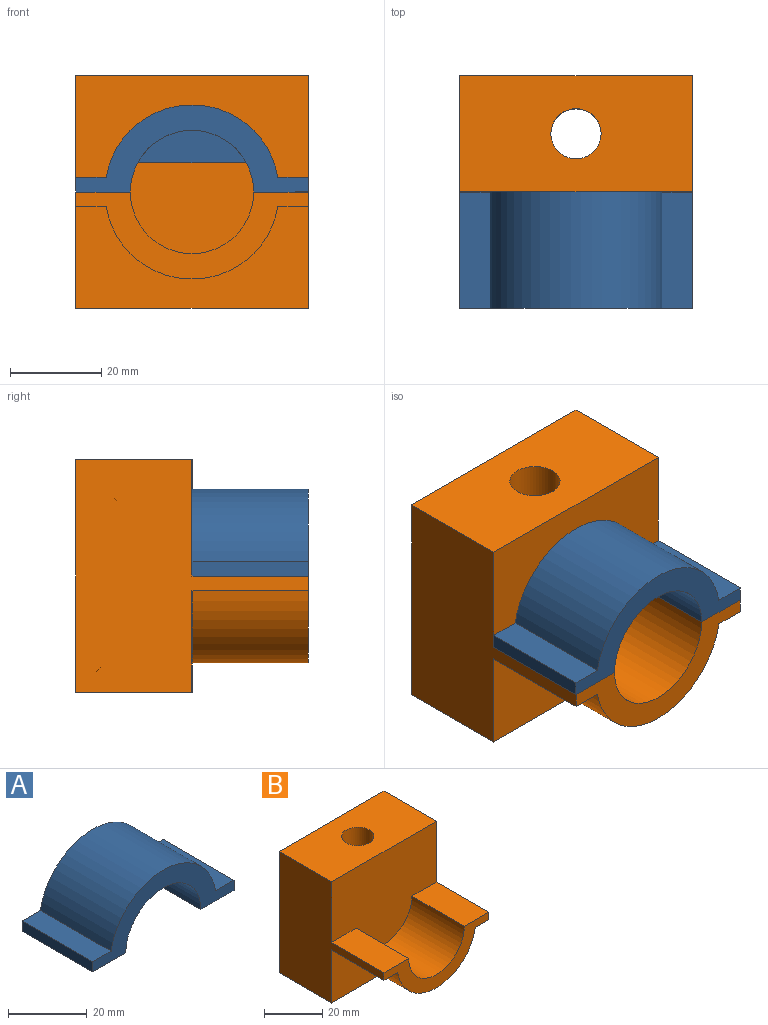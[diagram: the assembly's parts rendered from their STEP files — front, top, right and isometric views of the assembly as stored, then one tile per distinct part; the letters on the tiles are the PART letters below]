
ASSEMBLY  parts=2 mates=1
PART A: 13 faces, bbox 50.8x25.4x19.1 mm
  f0: cylinder r=13.49mm len=26.97mm, axis (0,1,0), area 891.2mm2, adj f1,f7,f8,f9,f10,f11,f12
  f1: plane 25.4x11.91mm, normal (0,0,-1), area 302.6mm2, adj f0,f2,f8,f9
  f2: plane 25.4x3.18mm, normal (1,0,0), area 80.6mm2, adj f1,f3,f8,f9
  f3: plane 25.4x6.62mm, normal (0,0,1), area 168.1mm2, adj f2,f4,f8,f9
  f4: cylinder r=19.05mm len=37.57mm, axis (0,1,0), area 1358.1mm2, adj f3,f5,f8,f9
  f5: plane 25.4x6.62mm, normal (0,0,1), area 168.1mm2, adj f4,f6,f8,f9
  f6: plane 25.4x3.18mm, normal (-1,0,0), area 80.6mm2, adj f5,f7,f8,f9
  f7: plane 25.4x11.91mm, normal (0,0,-1), area 302.6mm2, adj f0,f6,f8,f9
  f8: plane 50.8x19.05mm, normal (0,-1,0), area 325.2mm2, adj f0,f1,f2,f3,f4,f5,f6,f7
  f9: plane 50.8x19.05mm, normal (0,1,0), area 325.2mm2, adj f0,f1,f2,f3,f4,f5,f6,f7
  f10: plane 23.8x7.14mm, normal (0,-1,0), area 121mm2, adj f0,f12
  f11: plane 23.8x7.14mm, normal (0,1,0), area 121mm2, adj f0,f12
  f12: plane 23.8x6.35mm, normal (0,0,-1), area 151.1mm2, adj f0,f10,f11
PART B: 22 faces, bbox 50.8x50.8x50.8 mm
  f0: cylinder r=5.49mm len=44.45mm, axis (0,0,1), area 1534.1mm2, adj f4,f15
  f1: plane 50.8x22.23mm, normal (0,-1,0), area 679.4mm2, adj f3,f5,f6,f11,f12,f13
  f2: plane 50.8x38.89mm, normal (0,-1,0), area 1576.1mm2, adj f3,f4,f5,f8,f9,f10
  f3: plane 50.8x50.8mm, normal (1,0,0), area 1371mm2, adj f1,f2,f4,f6,f7,f8,f13,f14
  f4: plane 50.8x25.4mm, normal (0,0,1), area 1195.5mm2, adj f0,f2,f3,f5,f7
  f5: plane 50.8x50.8mm, normal (-1,0,0), area 1371mm2, adj f1,f2,f4,f6,f7,f10,f11,f14
  f6: plane 50.8x25.4mm, normal (0,0,-1), area 1079mm2, adj f1,f3,f5,f7,f16,f17,f18,f19
  f7: plane 50.8x50.8mm, normal (0,1,0), area 2580.6mm2, adj f3,f4,f5,f6
  f8: plane 25.4x11.91mm, normal (0,0,1), area 302.6mm2, adj f2,f3,f9,f14
  f9: cylinder r=13.49mm len=26.97mm, axis (0,1,0), area 1076.2mm2, adj f2,f8,f10,f14
  f10: plane 25.4x11.91mm, normal (0,0,1), area 302.6mm2, adj f2,f5,f9,f14
  f11: plane 25.4x6.62mm, normal (0,0,-1), area 168.1mm2, adj f1,f5,f12,f14
  f12: cylinder r=19.05mm len=37.57mm, axis (0,1,0), area 1358.1mm2, adj f1,f11,f13,f14
  f13: plane 25.4x6.62mm, normal (0,0,-1), area 168.1mm2, adj f1,f3,f12,f14
  f14: plane 50.8x19.05mm, normal (0,-1,0), area 325.2mm2, adj f3,f5,f8,f9,f10,f11,f12,f13
  f15: plane 18.04x15.62mm, normal (0,0,-1), area 116.5mm2, adj f0,f16,f17,f18,f19,f20,f21
  f16: plane 9.02x6.35mm, normal (-1,0,0), area 57.3mm2, adj f6,f15,f17,f21
  f17: plane 7.81x6.35mm, normal (-0.5,0.87,0), area 57.3mm2, adj f6,f15,f16,f18
  f18: plane 7.81x6.35mm, normal (0.5,0.87,0), area 57.3mm2, adj f6,f15,f17,f19
  f19: plane 9.02x6.35mm, normal (1,0,0), area 57.3mm2, adj f6,f15,f18,f20
  f20: plane 7.81x6.35mm, normal (0.5,-0.87,0), area 57.3mm2, adj f6,f15,f19,f21
  f21: plane 7.81x6.35mm, normal (-0.5,-0.87,0), area 57.3mm2, adj f6,f15,f16,f20
PLACE A t=(-5.12,-18.28,-3.94)mm
PLACE B t=(-5.12,7.12,-3.94)mm fixed
MATE fastened A.f7 <-> B.f10  axis (0,0,-1) through (-24.57,-18.28,-3.94)mm
